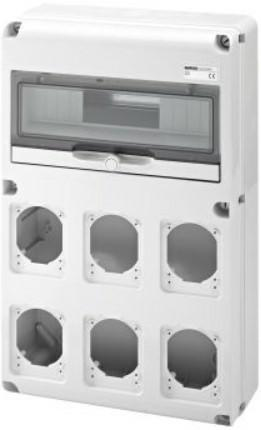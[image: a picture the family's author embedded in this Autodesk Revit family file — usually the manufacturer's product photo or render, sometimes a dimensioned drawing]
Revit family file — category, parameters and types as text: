
# Revit family: Building-IEC309Boards-GEWISS-68QDIN-DISTRIBUTION-BOARD-14MOD_6SOCKET-OUTLETS
name_source: partatom
category: Apparecchi elettrici
units: mm (PartAtom-declared; Revit-internal decimal feet)

## family parameters
Condiviso = No
Host = Superficie
Mantenere orientamento annotazione = Sì
Punto di calcolo locali = Sì
Quota connettore circolare = Usa diametro
Taglio con vuoti quando caricato = No
Tipo di parte = Normale

## types (1)
- GW68008N - Q-DIN 14M 6 FLANGES S.O.16/32A IP65
    Accordance with Standards = EN 60208 - EN 60670-1 - IEC 60670-24
    Catalogue = BUILDING
    Catalogue Range = 68 QDIN
    Colour = Grey RAL 7035
    Descrizione = Q-DIN 14M 6 FLANGES S.O.16/32A IP65
    Dispersible power A (W) = 24
    Dispersible power B (W) = 64
    EAN code = 8011564744790
    Electrocod = 2242
    Glow Wire Test = 650°C
    Houseable socket = 6 IEC 309 16/32A IP44/67
    IDF = 9b655afc-3a9b-4322-ac88-5a8dda757134
    IDT = cecb3bd3-e102-49fc-acd3-cb7b24533741
    IP degree = IP65
    Immagine tipo = GW68008N.jpg
    Installation type = Surface-mounting
    Insulation class = II
    Modello = GW68008N
    No. of modules EN 50022 = 14
    No. of provided blank lids = 2 IEC 16/32A
    Operating temperature: = -25 +40 °C
    POMELLO = bianco
    PRESA = rosso
    Produttore = GEWISS S.p.A.
    Prospetto di default = 1219 mm
    SEO = Board
    STRUTTURA = RAL - 7035
    STRUTTURA ALTA = Poche
    Shock resistance = IK08
    Spostamento_S = 1000 mm  [stored 3.28084 ft]
    Technical sheet = https://www.gewiss.com
    Thermo-pressure with ball = 70
    URL = https://www.gewiss.com
    VETRO = Vetro
    Version file RFA = 21.5
    Version type = Empty

note: source unit labels omitted for Thermo-pressure with ball — the stored unit's dimension contradicts the parameter name (converter mislabeling)

note: [stored X ft] marks values corroborated as IEEE doubles in the binary element streams (Revit-internal decimal feet)

## geometry (parser evidence)
native form markers: Sweep x4
no freeform markers — native parametric forms only
